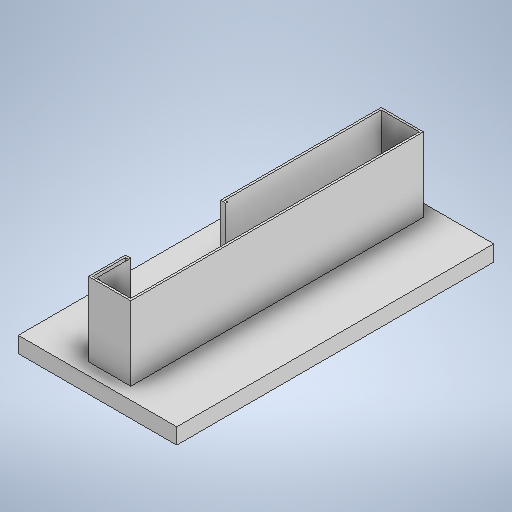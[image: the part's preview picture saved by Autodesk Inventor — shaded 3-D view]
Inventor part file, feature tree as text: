
AUTODESK INVENTOR PART (.ipt)
format: ipt  version: 2025.2 (Build 292293000, 293)  size: 624,128 bytes
history: native  units: mm
features: delete_face x4, extrude x3, sketch x2, shell x1, chamfer x1
ambient origin geometry x8: Origin, YZ Plane, XZ Plane, XY Plane, X Axis, Y Axis, Z Axis, Center Point
bodies: Solid1 (feature_tree), Solid2 (feature_tree)
feature tree (11):
  extrude  "Extrusion1"  Depth=300.0mm
  sketch  "Sketch2"  dims[d2=15.0mm d3=0.0mm d4=30.0mm d5=267.0mm d6=70.0mm d7=0.0mm d8=2.0mm d9=2.0mm d10=2.0mm d11=45.0deg d22=5.0mm d24=5.0mm d27=5.0mm d28=5.0mm d30=15.0mm d31=15.0mm d32=15.0mm d33=0.0mm d12=1.0mm d13=1.0mm d14=1.0mm d15=0.15mm d16=0.25mm d17=0.375mm d18=14.3117mm d19=0.75mm d20=20.594885mm d21=0.0625mm d23=0.375mm d29=0.5mm]
  extrude  "Extrusion2"  Depth=30.0mm
  shell  "Shell1"  Thickness=267.0mm
  chamfer  "Chamfer1"  Distance=70.0mm
  delete_face  "Delete Face1"
  delete_face  "Delete Face2"
  delete_face  "Delete Face3"
  delete_face  "Delete Face4"
  extrude  "Extrusion3"  Depth=2.0mm
  sketch  "Sketch1"  dims[d0=150.0mm d1=300.0mm]
